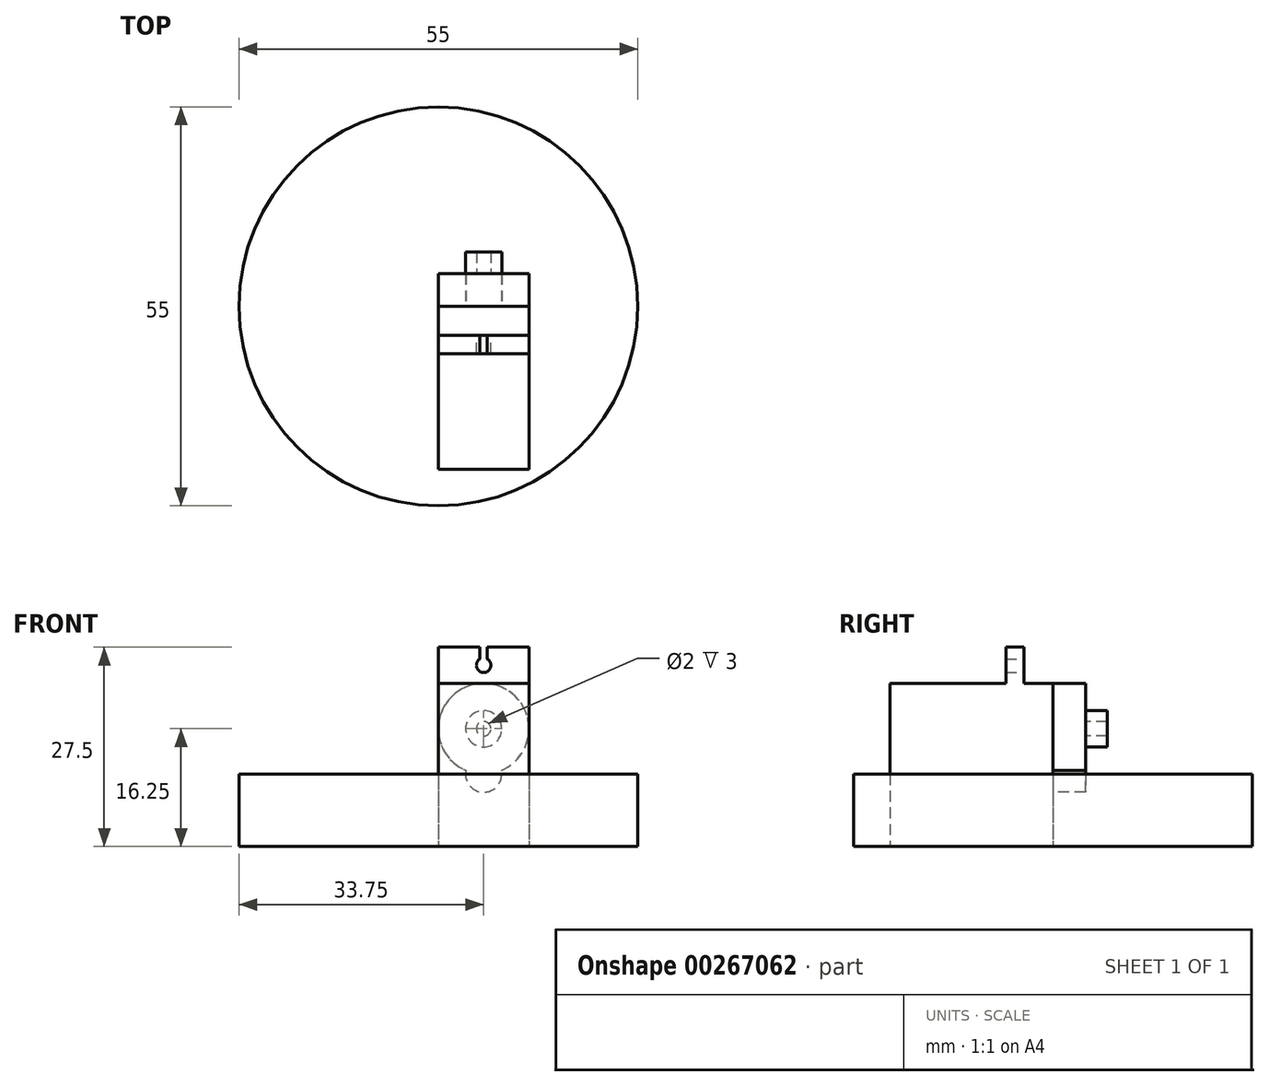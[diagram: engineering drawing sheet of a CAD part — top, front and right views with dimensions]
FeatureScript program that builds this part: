
annotation { "Feature Type Name" : "Feature", "Feature Type Description" : "" }
export const myFeature = defineFeature(function(context is Context, id is Id, definition is map)
    precondition{}
    {
        {
            var Q0;
            Q0=qCreatedBy(makeId("Top.planeOp"),FACE);
            var sketch = newSketch(context, id + "F0", { "sketchPlane" : qUnion([Q0])});
            skLineSegment(sketch, "E0.bottom", {"start": v(0, 0) * mm, "end": v(12.5, 0) * mm});
            skLineSegment(sketch, "E0.top", {"start": v(0, -22.5) * mm, "end": v(12.5, -22.5) * mm});
            skLineSegment(sketch, "E0.left", {"start": v(0, 0) * mm, "end": v(0, -22.5) * mm});
            skLineSegment(sketch, "E0.right", {"start": v(12.5, 0) * mm, "end": v(12.5, -22.5) * mm});
            skSolve(sketch);
        }
        {
            var Q0;
            Q0 = qSketchRegion(id + "F0", true);
            extrude(context, id + "F1", {"entities" : qUnion([Q0]), "depth" : 22.5 * mm});
        }
        {
            var Q0;
            Q0=makeQuery(id+"F1.opExtrude","CAP_FACE",FACE,{"disambiguationData":[OSD([sQuery(id+"F0.wireOp",EDGE,"E0.bottom"),sQuery(id+"F0.wireOp",EDGE,"E0.top"),sQuery(id+"F0.wireOp",EDGE,"E0.left"),sQuery(id+"F0.wireOp",EDGE,"E0.right")])],"isStart":false});
            var sketch = newSketch(context, id + "F2", { "sketchPlane" : qUnion([Q0])});
            skLineSegment(sketch, "E1.bottom", {"start": v(0, -4) * mm, "end": v(12.5, -4) * mm});
            skLineSegment(sketch, "E1.top", {"start": v(0, -6.5) * mm, "end": v(12.5, -6.5) * mm});
            skLineSegment(sketch, "E1.left", {"start": v(0, -4) * mm, "end": v(0, -6.5) * mm});
            skLineSegment(sketch, "E1.right", {"start": v(12.5, -4) * mm, "end": v(12.5, -6.5) * mm});
            skSolve(sketch);
        }
        {
            var Q0;
            Q0 = qSketchRegion(id + "F2", true);
            extrude(context, id + "F3", {"entities" : qUnion([Q0]), "operationType" : NewBodyOperationType.ADD, "depth" : 5 * mm});
        }
        {
            var Q0;
            Q0=makeQuery(id+"F3.opExtrude","SWEPT_FACE",FACE,{"disambiguationData":[OSD([sQuery(id+"F2.wireOp",EDGE,"E1.bottom")])]});
            var sketch = newSketch(context, id + "F4", { "sketchPlane" : qUnion([Q0])});
            skCircle(sketch, "E2", {"center": v(-6.25, 25) * mm, "radius": 1 * mm});
            skLineSegment(sketch, "E3.bottom", {"start": v(-6.75, 27.5) * mm, "end": v(-5.75, 27.5) * mm});
            skLineSegment(sketch, "E3.top", {"start": v(-6.75, 25) * mm, "end": v(-5.75, 25) * mm});
            skLineSegment(sketch, "E3.left", {"start": v(-6.75, 27.5) * mm, "end": v(-6.75, 25) * mm});
            skLineSegment(sketch, "E3.right", {"start": v(-5.75, 27.5) * mm, "end": v(-5.75, 25) * mm});
            skSolve(sketch);
        }
        {
            var Q0;
            Q0 = qSketchRegion(id + "F4", true);
            extrude(context, id + "F5", {"entities" : qUnion([Q0]), "operationType" : NewBodyOperationType.REMOVE, "endBound" : BoundingType.THROUGH_ALL, "oppositeDirection" : true, "depth" : 25 * mm});
        }
        {
            var Q0;
            Q0=makeQuery(id+"F1.opExtrude","SWEPT_FACE",FACE,{"disambiguationData":[OSD([sQuery(id+"F0.wireOp",EDGE,"E0.bottom")])]});
            var sketch = newSketch(context, id + "F6", { "sketchPlane" : qUnion([Q0])});
            skCircle(sketch, "E4", {"center": v(-6.25, 16.25) * mm, "radius": 6.25 * mm});
            skCircle(sketch, "E5", {"center": v(-6.25, 10) * mm, "radius": 2.5 * mm});
            skSolve(sketch);
        }
        {
            var Q0;
            Q0 = qSketchRegion(id + "F6", true);
            extrude(context, id + "F7", {"entities" : qUnion([Q0]), "operationType" : NewBodyOperationType.ADD, "depth" : 4.5 * mm});
        }
        {
            var Q0;
            Q0=makeQuery(id+"F7.opExtrude","CAP_FACE",FACE,{"disambiguationData":[OSD([sQuery(id+"F6.wireOp",EDGE,"E4")])],"isStart":false});
            var sketch = newSketch(context, id + "F8", { "sketchPlane" : qUnion([Q0])});
            skCircle(sketch, "E6", {"center": v(-6.25, 16.25) * mm, "radius": 2.5 * mm});
            skCircle(sketch, "E7", {"center": v(-6.25, 16.25) * mm, "radius": 1 * mm});
            skSolve(sketch);
        }
        {
            var Q0;
            Q0=makeQuery(id+"F8.imprint","IMPRINT",FACE,{"disambiguationData":[TD([[makeQuery(id+"F8.imprint","IMPRINT",EDGE,{"derivedFrom":sQuery(id+"F8.wireOp",EDGE,"E6")}),1.0]])]});
            extrude(context, id + "F9", {"entities" : qUnion([Q0]), "operationType" : NewBodyOperationType.ADD, "depth" : 3 * mm});
        }
        {
            var Q0;
            Q0=qCreatedBy(makeId("Top.planeOp"),FACE);
            cPlane(context, id + "F10", {"entities" : qUnion([Q0]), "cplaneType" : CPlaneType.OFFSET, "offset" : 11.25 * mm, "width" : 150 * mm, "height" : 150 * mm});
        }
        {
            var Q0;
            Q0=qCreatedBy(makeId("Top.planeOp"),FACE);
            var sketch = newSketch(context, id + "F11", { "sketchPlane" : qUnion([Q0])});
            skCircle(sketch, "E8", {"center": v(0, 0) * mm, "radius": 27.5 * mm});
            skSolve(sketch);
        }
        {
            var Q0;
            Q0 = qSketchRegion(id + "F11", true);
            extrude(context, id + "F12", {"entities" : qUnion([Q0]), "depth" : 10 * mm});
        }
    });
